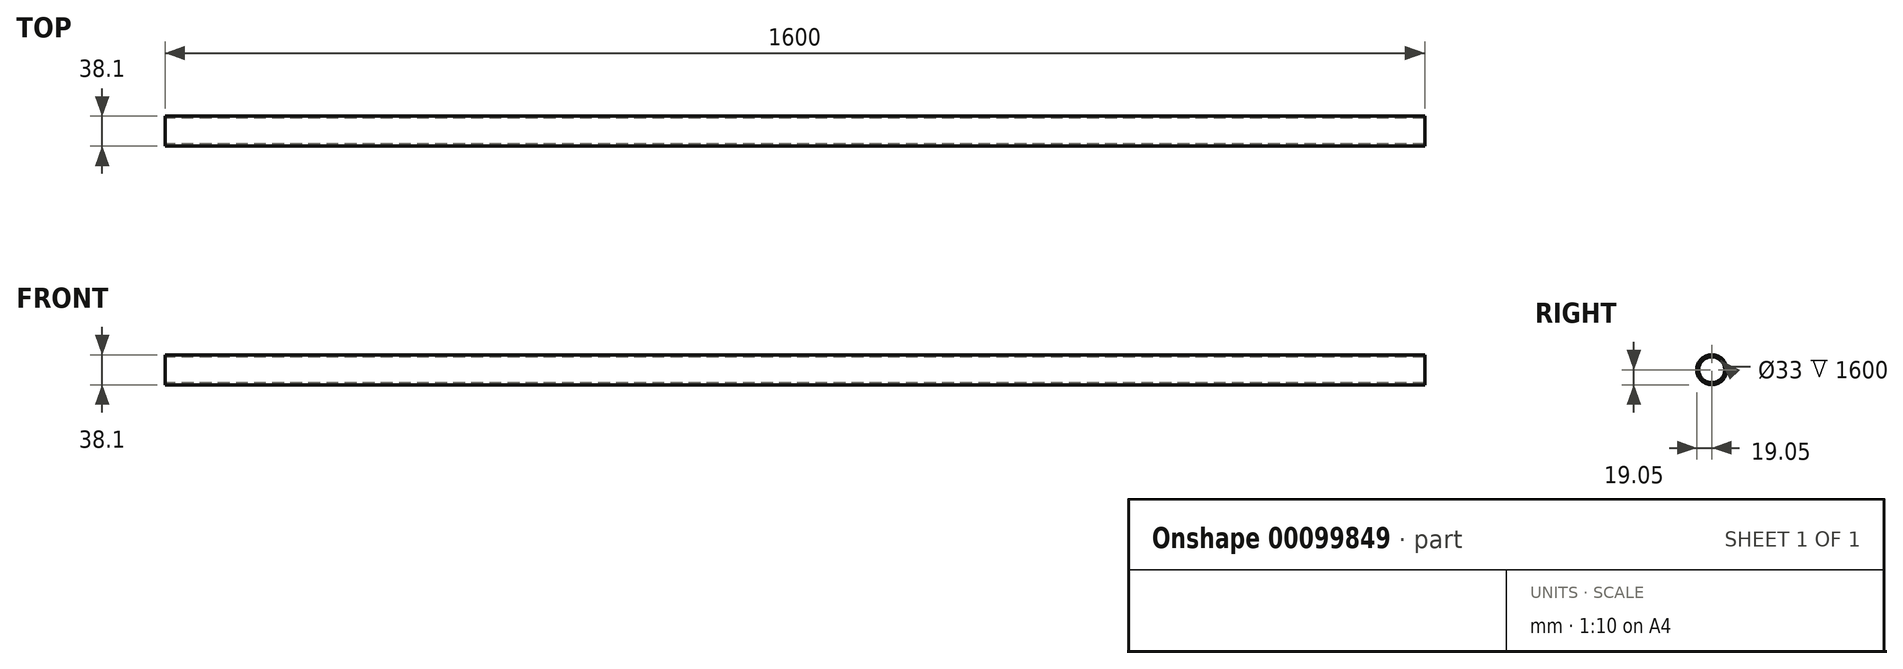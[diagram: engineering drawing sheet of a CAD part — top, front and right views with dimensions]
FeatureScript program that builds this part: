
annotation { "Feature Type Name" : "Feature", "Feature Type Description" : "" }
export const myFeature = defineFeature(function(context is Context, id is Id, definition is map)
    precondition{}
    {
        {
            var Q0;
            Q0=qCreatedBy(makeId("Right.planeOp"),FACE);
            var sketch = newSketch(context, id + "F0", { "sketchPlane" : qUnion([Q0])});
            skCircle(sketch, "E0", {"center": v(0, 0) * mm, "radius": 19.05 * mm});
            skCircle(sketch, "E1", {"center": v(0, 0) * mm, "radius": 16.5 * mm});
            skSolve(sketch);
        }
        {
            var Q0;
            Q0=qSketchRegion(id+"F0",true);
            extrude(context, id + "F1", {"entities" : qUnion([Q0]), "endBound" : BoundingType.SYMMETRIC, "depth" : 1600 * mm});
        }
    });
